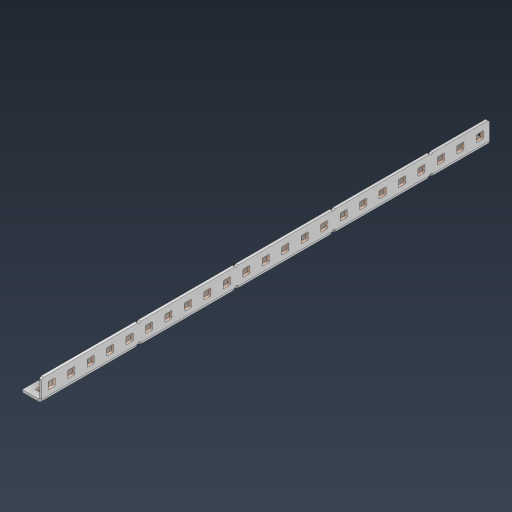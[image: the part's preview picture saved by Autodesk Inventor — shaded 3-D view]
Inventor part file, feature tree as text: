
AUTODESK INVENTOR PART (.ipt)
format: ipt  version: 2024.3 (Build 283343000, 343)  size: 948,224 bytes
history: native  units: in
note: dims shown in document units (in); Inventor stores cm internally (conversion verified against a paired STEP export)
features: other x76, extrude x67, sheet_metal_op x11, pattern_linear x2, mirror x1, chamfer x1, sketch x1
ambient origin geometry x8: Origin, YZ Plane, XZ Plane, XY Plane, X Axis, Y Axis, Z Axis, Center Point
bodies: Solid1 (feature_tree), Body (feature_tree)
feature tree (159):
  sheet_metal_op  "Flanges"
  other  "Flange Pattern Plane"
  other  "Flange Pattern Sketch"
  sheet_metal_op  "Flange Pattern"
  sheet_metal_op  "Body Pattern"
  pattern_linear  "Center Pattern"  Spacing1=11.5in  [1 undecoded]
  other  "Arc Length"
  mirror  "Notch Mirror"
  pattern_linear  "Notch Pattern"  Spacing1=0.0625in  [1 undecoded]
  chamfer  "End Chamfer"
  extrude  "Half Cut"  Depth=0.0625in
  other  "Plate1"
  sketch  "Sketch2"  dims[d0=1.0in d1=11.5in d2=0.0625in d3=0.0625in d4=0.0312in d5=0.125in d6=0.0625in d7=0.5in d8=90.0deg d9=0.0312in d10=0.25in d11=0.0625in d12=0.0625in d16=0.182in d17=0.02in d18=0.0625in d19=0.0in d20=0.25in d21=0.25in d38=9.0551in d40=0.5in d41=0.3937in d43=1.0in d46=0.172in d47=1.0in d48=0.0in d49=0.182in d50=0.02in d51=0.25in d52=0.25in d53=0.0625in d54=0.0in d55=0.172in d56=1.0in d57=0.0in d58=0.25in d60=9.0551in d62=0.5in d63=0.3937in d65=0.5in d85=0.1473in d86=0.1782in d88=0.04in d89=0.0625in d90=0.0in d91=0.04in d92=0.0491in d95=2.5in d96=0.04in d97=0.25in d98=45.0deg d99=0.25in d100=0.5in d101=0.0in d102=2.497in d106=0.182in d107=0.02in d108=0.5in d109=0.5in d110=0.0625in d111=0.0in d112=0.172in d113=0.5in d114=0.0in d117=0.5in d118=0.5in d119=0.5in]
  other  "Plate2"
  sheet_metal_op  "Bend1"
  sheet_metal_op  "Corner1"
  other  "Srf1"
  other  "Srf2"
  other  "Srf91"
  sheet_metal_op  "Body Pattern Sketch"
  other  "Srf92"
  other  "Srf786"
  other  "Srf823"
  other  "Srf824"
  other  "Srf825"
  other  "Srf826"
  other  "Srf827"
  other  "Srf828"
  other  "Srf829"
  other  "Srf856"
  other  "Srf857"
  other  "Srf858"
  other  "Srf859"
  other  "Srf860"
  other  "Srf861"
  other  "Srf862"
  other  "Srf889"
  other  "Srf890"
  other  "Srf891"
  other  "Srf892"
  other  "Srf893"
  other  "Srf894"
  other  "Srf895"
  other  "Srf896"
  other  "Srf922"
  other  "Srf923"
  other  "Srf924"
  other  "Srf925"
  other  "Srf926"
  other  "Srf959"
  other  "Srf960"
  other  "Srf961"
  other  "Srf962"
  other  "Srf963"
  other  "Srf996"
  other  "Srf997"
  other  "Srf998"
  other  "Srf999"
  other  "Srf1000"
  other  "Srf1143"
  other  "Srf1144"
  other  "Srf1145"
  other  "Srf1146"
  other  "Srf1147"
  other  "Srf1148"
  other  "Srf1149"
  other  "Srf1150"
  other  "Srf1151"
  other  "Srf1199"
  other  "Srf1200"
  other  "Srf1201"
  other  "Srf1202"
  other  "Srf1203"
  other  "Srf1204"
  other  "Srf1205"
  other  "Srf1206"
  other  "Srf1207"
  other  "Srf1255"
  other  "Srf1256"
  other  "Srf1257"
  other  "Srf1258"
  other  "Srf1259"
  other  "Srf1260"
  other  "Srf1261"
  other  "Srf1262"
  other  "Srf1263"
  sheet_metal_op  "Flange Stamp"
  sheet_metal_op  "Flange Circle"
  sheet_metal_op  "Body Stamp"
  sheet_metal_op  "Body Circle"
  other  "Center Stamp"
  other  "Center Circle"
  sheet_metal_op  "Notch"
  extrude  "ExtrusionSrf2"  Depth=0.0312in
  extrude  "ExtrusionSrf92"  Depth=0.5in
  extrude  "ExtrusionSrf823"  Depth=0.0625in
  extrude  "ExtrusionSrf824"  Depth=0.5in TaperAngle=90.0deg
  extrude  "ExtrusionSrf825"  Depth=0.5in
  extrude  "ExtrusionSrf826"  Depth=0.0625in
  extrude  "ExtrusionSrf827"  Depth=0.0625in
  extrude  "ExtrusionSrf828"  Depth=0.182in
  extrude  "ExtrusionSrf829"  Depth=0.02in
  extrude  "ExtrusionSrf856"  Depth=0.0625in
  extrude  "ExtrusionSrf857"  TaperAngle=0.0deg  [1 undecoded]
  extrude  "ExtrusionSrf858"  Depth=0.5in
  extrude  "ExtrusionSrf859"  Depth=0.5in
  extrude  "ExtrusionSrf860"  Depth=0.5in
  extrude  "ExtrusionSrf861"  Depth=0.5in
  extrude  "ExtrusionSrf862"  Depth=1.0in TaperAngle=0.0deg
  extrude  "ExtrusionSrf889"  Depth=0.182in
  extrude  "ExtrusionSrf890"  Depth=0.02in
  extrude  "ExtrusionSrf891"  Depth=0.5in
  extrude  "ExtrusionSrf892"  Depth=0.5in
  extrude  "ExtrusionSrf893"  Depth=0.0625in
  extrude  "ExtrusionSrf894"  TaperAngle=0.0deg  [1 undecoded]
  extrude  "ExtrusionSrf895"  Depth=0.5in
  extrude  "ExtrusionSrf896"  Depth=1.0in TaperAngle=0.0deg
  extrude  "ExtrusionSrf922"  Depth=0.5in
  extrude  "ExtrusionSrf923"  Depth=0.5in
  extrude  "ExtrusionSrf924"  Depth=0.5in
  extrude  "ExtrusionSrf925"  Depth=0.5in
  extrude  "ExtrusionSrf926"  Depth=0.5in
  extrude  "ExtrusionSrf959"  Depth=0.5in
  extrude  "ExtrusionSrf960"  Depth=0.0625in
  extrude  "ExtrusionSrf961"  TaperAngle=0.0deg  [1 undecoded]
  extrude  "ExtrusionSrf962"  Depth=0.5in
  extrude  "ExtrusionSrf963"  Depth=0.5in
  extrude  "ExtrusionSrf996"  Depth=0.5in
  extrude  "ExtrusionSrf997"  Depth=0.5in TaperAngle=45.0deg
  extrude  "ExtrusionSrf998"  Depth=0.5in
  extrude  "ExtrusionSrf999"  Depth=0.5in TaperAngle=0.0deg
  extrude  "ExtrusionSrf1000"  Depth=0.5in
  extrude  "ExtrusionSrf1143"  Depth=0.182in
  extrude  "ExtrusionSrf1144"  Depth=0.02in
  extrude  "ExtrusionSrf1145"  Depth=0.5in
  extrude  "ExtrusionSrf1146"  Depth=0.5in
  extrude  "ExtrusionSrf1147"  Depth=0.0625in
  extrude  "ExtrusionSrf1148"  TaperAngle=0.0deg  [1 undecoded]
  extrude  "ExtrusionSrf1149"  Depth=0.5in
  extrude  "ExtrusionSrf1150"  Depth=0.5in TaperAngle=0.0deg
  extrude  "ExtrusionSrf1151"  Depth=0.5in
  extrude  "ExtrusionSrf1199"  Depth=0.5in
  extrude  "ExtrusionSrf1200"  Depth=0.5in
  extrude  "ExtrusionSrf1201"  [1 undecoded]
  extrude  "ExtrusionSrf1202"  [1 undecoded]
  extrude  "ExtrusionSrf1203"  [1 undecoded]
  extrude  "ExtrusionSrf1204"  [1 undecoded]
  extrude  "ExtrusionSrf1205"  [1 undecoded]
  extrude  "ExtrusionSrf1206"  [1 undecoded]
  extrude  "ExtrusionSrf1207"  [1 undecoded]
  extrude  "ExtrusionSrf1255"  [1 undecoded]
  extrude  "ExtrusionSrf1256"  [1 undecoded]
  extrude  "ExtrusionSrf1257"  [1 undecoded]
  extrude  "ExtrusionSrf1258"  [1 undecoded]
  extrude  "ExtrusionSrf1259"  [1 undecoded]
  extrude  "ExtrusionSrf1260"  [1 undecoded]
  extrude  "ExtrusionSrf1261"  [1 undecoded]
  extrude  "ExtrusionSrf1262"  [1 undecoded]
  extrude  "ExtrusionSrf1263"  [1 undecoded]
note: 22 required parameter values undecoded (feature->parameter linkage not recoverable at this tier; creation-order binding heuristic only, values carry confidence <= 0.55)
